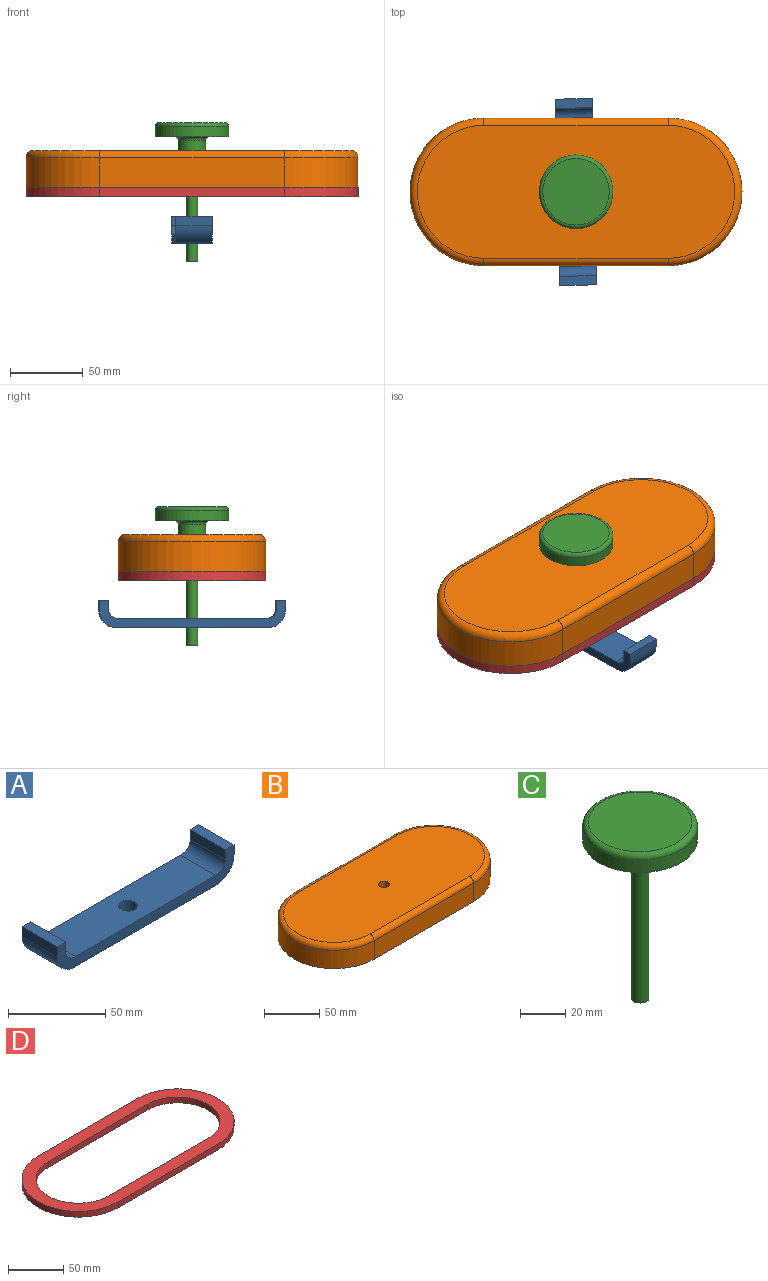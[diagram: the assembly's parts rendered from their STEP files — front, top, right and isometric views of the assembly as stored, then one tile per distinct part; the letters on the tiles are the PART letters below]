
ASSEMBLY  parts=4 mates=4
PART A: 15 faces, bbox 128.4x25.4x18.9 mm
  f0: cylinder r=12.7mm len=25.4mm, axis (0,1,0), area 520.9mm2, adj f1,f11,f12,f13
  f1: plane 101.6x25.4mm, normal (0,0,-1), area 2509.4mm2, adj f0,f2,f12,f13,f14
  f2: cylinder r=12.7mm len=25.4mm, axis (0,1,0), area 520.9mm2, adj f1,f3,f12,f13
  f3: plane 25.4x6.35mm, normal (1,0,0), area 161.3mm2, adj f2,f4,f12,f13
  f4: plane 25.4x6.35mm, normal (0,0,1), area 161.3mm2, adj f3,f5,f12,f13
  f5: plane 25.4x6.31mm, normal (-1,0,0), area 160.3mm2, adj f4,f6,f12,f13
  f6: cylinder r=6.35mm len=25.4mm, axis (0,1,0), area 263.4mm2, adj f5,f7,f12,f13
  f7: plane 102.01x25.4mm, normal (0,0,1), area 2519.7mm2, adj f6,f8,f12,f13,f14
  f8: cylinder r=6.35mm len=25.4mm, axis (0,1,0), area 263.4mm2, adj f7,f9,f12,f13
  f9: plane 25.4x6.31mm, normal (1,0,0), area 160.3mm2, adj f8,f10,f12,f13
  f10: plane 25.4x6.35mm, normal (0,0,1), area 161.3mm2, adj f9,f11,f12,f13
  f11: plane 25.4x6.35mm, normal (-1,0,0), area 161.3mm2, adj f0,f10,f12,f13
  f12: plane 128.39x18.91mm, normal (0,-1,0), area 922.9mm2, adj f0,f1,f2,f3,f4,f5,f6,f7
  f13: plane 128.39x18.91mm, normal (0,1,0), area 922.9mm2, adj f0,f1,f2,f3,f4,f5,f6,f7
  f14: cylinder r=4.76mm len=9.53mm, axis (0,0,1), area 190mm2, adj f1,f7
PART B: 16 faces, bbox 237x110x25.4 mm
  f0: plane 228.6x101.6mm, normal (0,0,-1), area 6772.8mm2, adj f1,f2,f3,f4,f6,f7,f8,f9
  f1: cylinder r=50.8mm len=101.6mm, axis (0,0,-1), area 3242.9mm2, adj f0,f2,f4,f13
  f2: plane 127x20.32mm, normal (0,1,0), area 2580.6mm2, adj f0,f1,f3,f14
  f3: cylinder r=50.8mm len=101.6mm, axis (0,0,-1), area 3242.9mm2, adj f0,f2,f4,f12
  f4: plane 127x20.32mm, normal (0,-1,0), area 2580.6mm2, adj f0,f1,f3,f11
  f5: plane 218.44x91.44mm, normal (0,0,1), area 18108.6mm2, adj f11,f12,f13,f14,f15
  f6: cylinder r=38.1mm len=76.2mm, axis (0,0,-1), area 2280.2mm2, adj f0,f7,f9,f10
  f7: plane 127x19.05mm, normal (0,-1,0), area 2419.3mm2, adj f0,f6,f8,f10
  f8: cylinder r=38.1mm len=76.2mm, axis (0,0,-1), area 2280.2mm2, adj f0,f7,f9,f10
  f9: plane 127x19.05mm, normal (0,1,0), area 2419.3mm2, adj f0,f6,f8,f10
  f10: plane 203.2x76.2mm, normal (0,0,-1), area 14166.5mm2, adj f6,f7,f8,f9,f15
  f11: cylinder r=5.08mm len=127mm, axis (-1,0,0), area 1013.4mm2, adj f4,f5,f12,f13
  f12: torus R=45.72mm, axis (0,0,1), area 1227.2mm2, adj f3,f5,f11,f14
  f13: torus R=45.72mm, axis (0,0,1), area 1227.2mm2, adj f1,f5,f11,f14
  f14: cylinder r=5.08mm len=127mm, axis (1,0,0), area 1013.4mm2, adj f2,f5,f12,f13
  f15: cylinder r=4.76mm len=9.53mm, axis (0,0,-1), area 190mm2, adj f5,f10
PART C: 9 faces, bbox 55x55x95.3 mm
  f0: cylinder r=3.97mm len=76.2mm, axis (0,0,1), area 1900.2mm2, adj f1,f3
  f1: plane 7.94x7.94mm, normal (0,0,-1), area 49.5mm2, adj f0
  f2: cylinder r=9.53mm len=19.05mm, axis (0,0,-1), area 418mm2, adj f3,f8
  f3: plane 19.05x19.05mm, normal (0,0,-1), area 235.5mm2, adj f0,f2
  f4: cylinder r=25.4mm len=50.8mm, axis (0,0,-1), area 1114.8mm2, adj f6,f7
  f5: plane 45.72x45.72mm, normal (0,0,1), area 1641.7mm2, adj f7
  f6: plane 50.8x50.8mm, normal (0,0,-1), area 1569.5mm2, adj f4,f8
  f7: torus R=22.86mm, axis (0,0,1), area 613.6mm2, adj f4,f5
  f8: torus R=12.06mm, axis (0,0,1), area 261.9mm2, adj f2,f6
PART D: 10 faces, bbox 228.6x101.6x6.4 mm
  f0: plane 127x6.35mm, normal (0,-1,0), area 806.5mm2, adj f1,f7,f8,f9
  f1: cylinder r=38.1mm len=76.2mm, axis (0,0,-1), area 760.1mm2, adj f0,f2,f8,f9
  f2: plane 127x6.35mm, normal (0,1,0), area 806.5mm2, adj f1,f7,f8,f9
  f3: cylinder r=50.8mm len=101.6mm, axis (0,0,-1), area 1013.4mm2, adj f4,f6,f8,f9
  f4: plane 127x6.35mm, normal (0,1,0), area 806.5mm2, adj f3,f5,f8,f9
  f5: cylinder r=50.8mm len=101.6mm, axis (0,0,-1), area 1013.4mm2, adj f4,f6,f8,f9
  f6: plane 127x6.35mm, normal (0,-1,0), area 806.5mm2, adj f3,f5,f8,f9
  f7: cylinder r=38.1mm len=76.2mm, axis (0,0,-1), area 760.1mm2, adj f0,f2,f8,f9
  f8: plane 228.6x101.6mm, normal (0,0,1), area 6772.8mm2, adj f0,f1,f2,f3,f4,f5,f6,f7
  f9: plane 228.6x101.6mm, normal (0,0,-1), area 6772.8mm2, adj f0,f1,f2,f3,f4,f5,f6,f7
PLACE A rot(axis=(0,0,-1),88.7deg) t=(32.32,62.66,-77.35)mm
PLACE B t=(32.32,62.66,-38.47)mm
PLACE C t=(32.32,62.66,-13.07)mm
PLACE D t=(34.25,65.84,-44.82)mm
MATE cylindrical A.f14 <-> C.f0  axis (0,0,1) through (32.32,62.66,-71)mm
MATE planar D.f8 <-> B.f0  axis (0,0,1) through (95.82,11.86,-38.47)mm
MATE planar C.f0 <-> B.f15  axis (0,0,-1) through (32.32,62.66,-13.07)mm
MATE cylindrical C.f0 <-> B.f15  axis (0,0,-1) through (32.32,62.66,-89.27)mm
